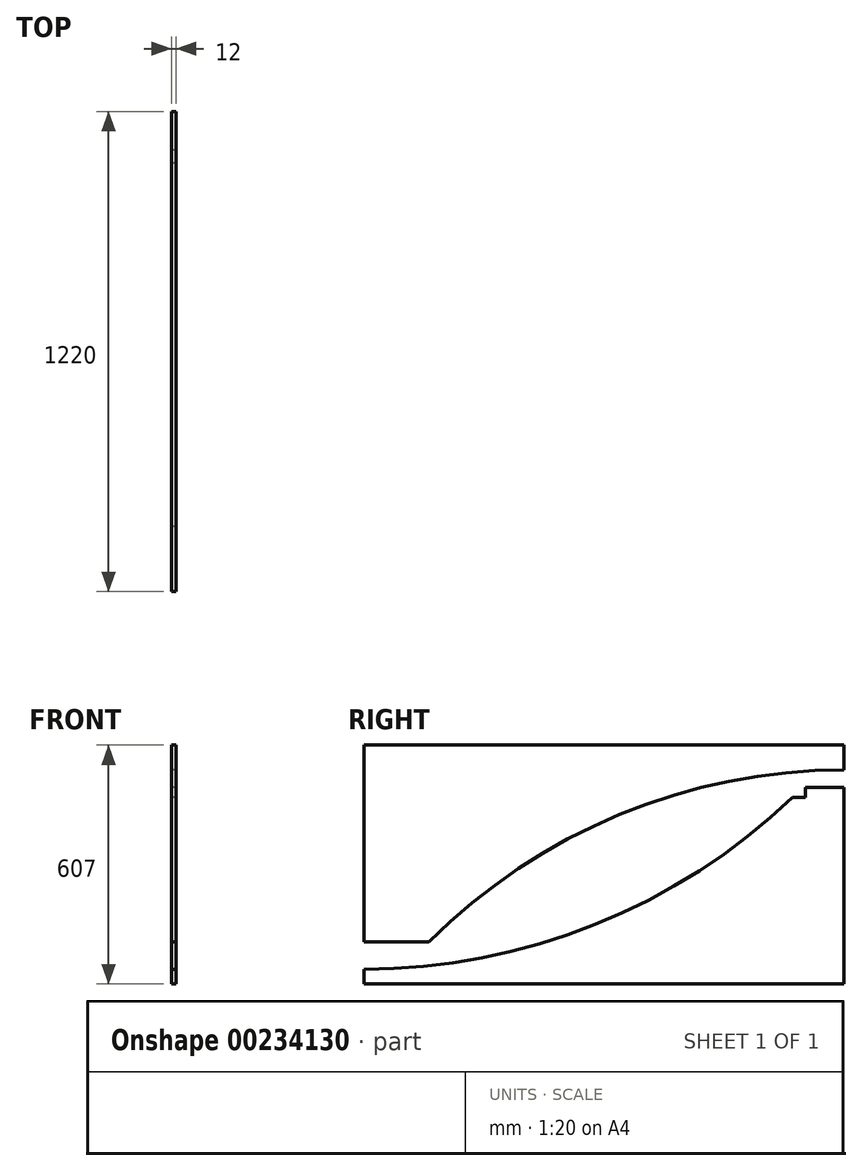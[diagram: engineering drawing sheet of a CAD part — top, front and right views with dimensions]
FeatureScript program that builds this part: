
annotation { "Feature Type Name" : "Feature", "Feature Type Description" : "" }
export const myFeature = defineFeature(function(context is Context, id is Id, definition is map)
    precondition{}
    {
        {
            var Q0;
            Q0=qCreatedBy(makeId("Right.planeOp"),FACE);
            var sketch = newSketch(context, id + "F0", { "sketchPlane" : qUnion([Q0])});
            skLineSegment(sketch, "E0", {"start": v(0, 0) * mm, "end": v(0, 500) * mm});
            skLineSegment(sketch, "E1", {"start": v(0, 500) * mm, "end": v(-98.17, 500) * mm});
            skLineSegment(sketch, "E2", {"start": v(0, 0) * mm, "end": v(-1104.63, 0) * mm});
            skArc(sketch, "E3", {"start": v(-711.8, 63.33) * mm, "mid": v(-374.8, 235.2) * mm, "end": v(-104.63, 500) * mm, "construction": true});
            skLineSegment(sketch, "E4", {"start": v(-1392.72, 38) * mm, "end": v(-868.93, 38) * mm, "construction": true});
            skPoint(sketch, "E5.visualSharp", {"position": v(-798.76, 38) * mm});
            skArc(sketch, "E5.filletArc", {"start": v(-868.93, 38) * mm, "mid": v(-789.35, 44.37) * mm, "end": v(-711.8, 63.33) * mm, "construction": true});
            skArc(sketch, "E6", {"start": v(-1220, 38) * mm, "mid": v(-633.6, 151.05) * mm, "end": v(-131.25, 474) * mm});
            skLineSegment(sketch, "E7", {"start": v(-104.63, 500) * mm, "end": v(-876.81, -272.18) * mm, "construction": true});
            skLineSegment(sketch, "E8.bottom", {"start": v(0, 0) * mm, "end": v(-1220, 0) * mm});
            skLineSegment(sketch, "E8.top", {"start": v(0, 607) * mm, "end": v(-1220, 607) * mm});
            skLineSegment(sketch, "E8.right", {"start": v(-1220, 0) * mm, "end": v(-1220, 38) * mm});
            skLineSegment(sketch, "E9", {"start": v(-1220, 107) * mm, "end": v(-1055.01, 107) * mm});
            skLineSegment(sketch, "E10", {"start": v(0, 544) * mm, "end": v(221.12, 544) * mm, "construction": true});
            skArc(sketch, "E11", {"start": v(0, 544) * mm, "mid": v(-570.97, 430.43) * mm, "end": v(-1055.01, 107) * mm});
            skLineSegment(sketch, "E12", {"start": v(-1055.01, 107) * mm, "end": v(-254.28, 907.73) * mm, "construction": true});
            skLineSegment(sketch, "E13.trimOffspring", {"start": v(0, 544) * mm, "end": v(0, 607) * mm});
            skLineSegment(sketch, "E14.trimOffspring", {"start": v(-1220, 107) * mm, "end": v(-1220, 607) * mm});
            skLineSegment(sketch, "E15", {"start": v(-98.17, 500) * mm, "end": v(-98.17, 474) * mm});
            skLineSegment(sketch, "E16", {"start": v(-98.17, 474) * mm, "end": v(-131.25, 474) * mm});
            skSolve(sketch);
        }
        {
            var Q0;
            Q0 = qSketchRegion(id + "F0", true);
            extrude(context, id + "F1", {"entities" : qUnion([Q0]), "depth" : 12 * mm});
        }
    });
